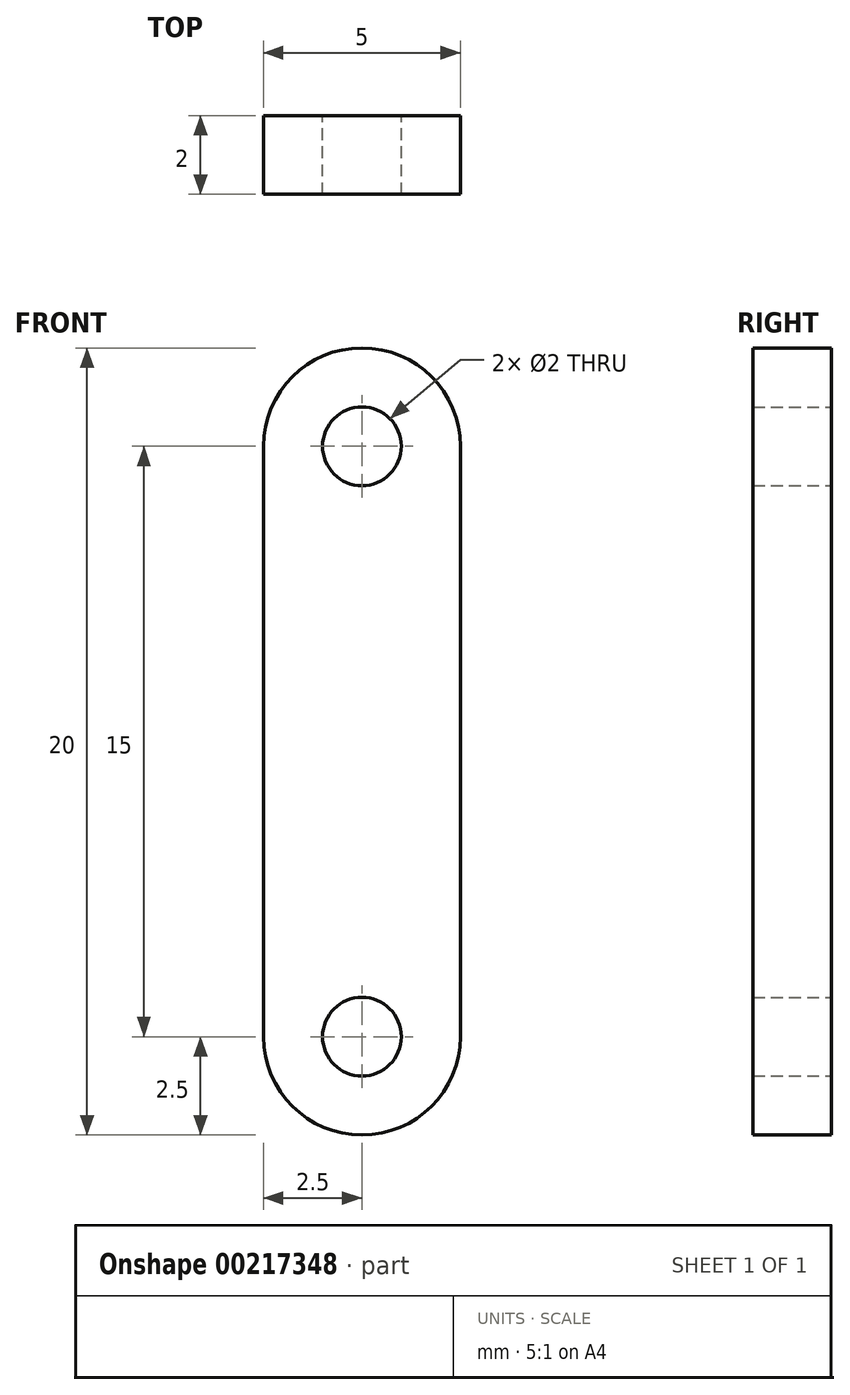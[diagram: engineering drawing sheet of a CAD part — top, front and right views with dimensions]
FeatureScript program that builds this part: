
annotation { "Feature Type Name" : "Feature", "Feature Type Description" : "" }
export const myFeature = defineFeature(function(context is Context, id is Id, definition is map)
    precondition{}
    {
        {
            var Q0;
            Q0=qCreatedBy(makeId("Front.planeOp"),FACE);
            var sketch = newSketch(context, id + "F0", { "sketchPlane" : qUnion([Q0])});
            skCircle(sketch, "E0", {"center": v(0, 0) * mm, "radius": 1 * mm});
            skArc(sketch, "E1", {"start": v(2.5, 0) * mm, "mid": v(0, 2.5) * mm, "end": v(-2.5, 0) * mm});
            skArc(sketch, "E2", {"start": v(-2.5, -15) * mm, "mid": v(0, -17.5) * mm, "end": v(2.5, -15) * mm});
            skLineSegment(sketch, "E3", {"start": v(-2.5, 0) * mm, "end": v(-2.5, -15) * mm});
            skLineSegment(sketch, "E4", {"start": v(2.5, 0) * mm, "end": v(2.5, -15) * mm});
            skCircle(sketch, "E5", {"center": v(0, -15) * mm, "radius": 1 * mm});
            skSolve(sketch);
        }
        {
            var Q0;
            Q0=makeQuery(id+"F0.imprint","IMPRINT",FACE,{"disambiguationData":[TD([[makeQuery(id+"F0.imprint","IMPRINT",EDGE,{"derivedFrom":sQuery(id+"F0.wireOp",EDGE,"E0")}),-1.0]])]});
            extrude(context, id + "F1", {"entities" : qUnion([Q0]), "depth" : 2 * mm});
        }
    });
